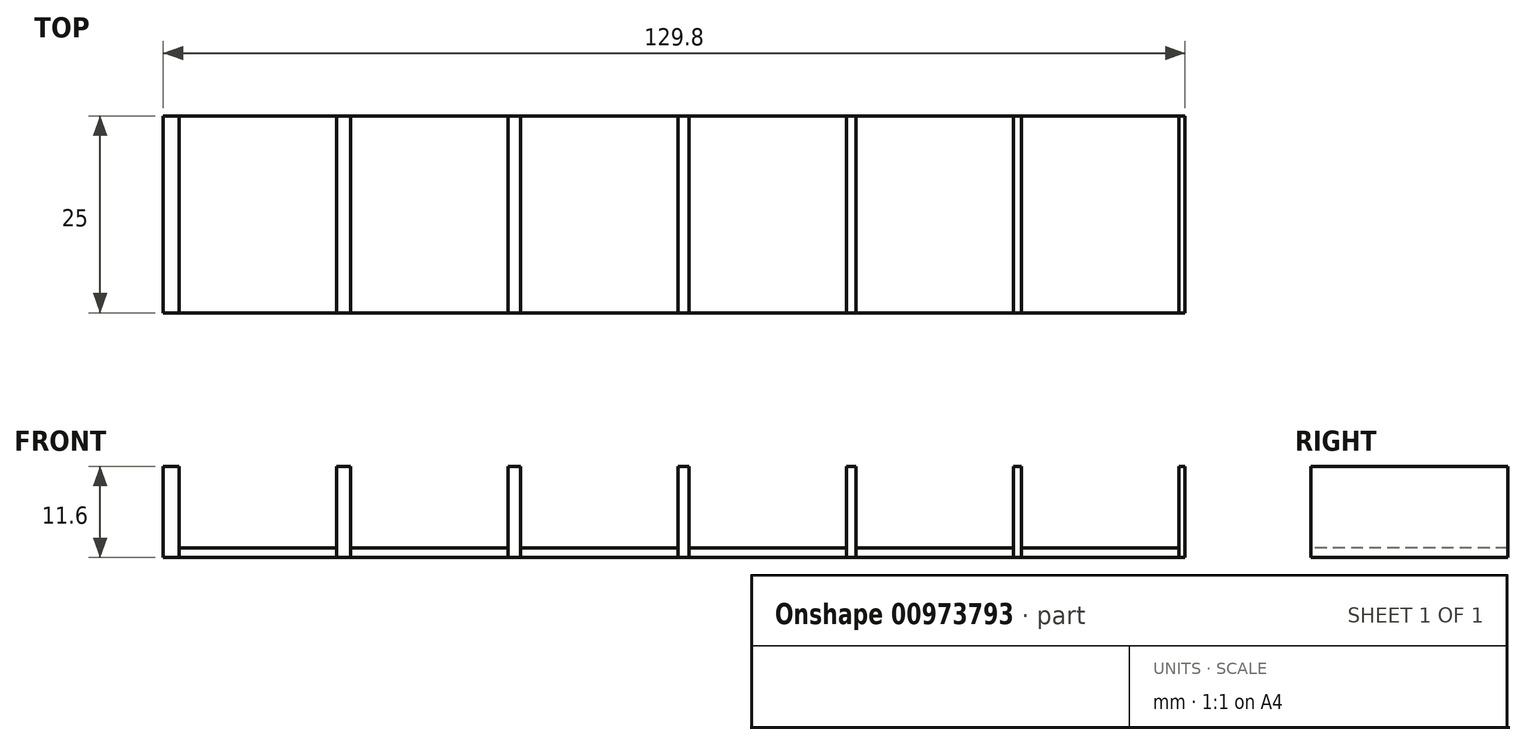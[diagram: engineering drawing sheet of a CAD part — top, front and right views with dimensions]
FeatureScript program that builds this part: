
annotation { "Feature Type Name" : "Feature", "Feature Type Description" : "" }
export const myFeature = defineFeature(function(context is Context, id is Id, definition is map)
    precondition{}
    {
        {
            var Q0;
            Q0=qCreatedBy(makeId("Top.planeOp"),FACE);
            var sketch = newSketch(context, id + "F0", { "sketchPlane" : qUnion([Q0])});
            skLineSegment(sketch, "E0.bottom", {"start": v(0, 0) * mm, "end": v(129.8, 0) * mm});
            skLineSegment(sketch, "E0.top", {"start": v(0, -25) * mm, "end": v(129.8, -25) * mm});
            skLineSegment(sketch, "E0.left", {"start": v(0, 0) * mm, "end": v(0, -25) * mm});
            skLineSegment(sketch, "E0.right", {"start": v(129.8, 0) * mm, "end": v(129.8, -25) * mm});
            skLineSegment(sketch, "E1.0", {"start": v(129, 0) * mm, "end": v(129, -25) * mm});
            skLineSegment(sketch, "E2.0", {"start": v(109, 0) * mm, "end": v(109, -25) * mm});
            skLineSegment(sketch, "E3.0", {"start": v(108, 0) * mm, "end": v(108, -25) * mm});
            skLineSegment(sketch, "E4.0", {"start": v(88, 0) * mm, "end": v(88, -25) * mm});
            skLineSegment(sketch, "E5.0", {"start": v(86.8, 0) * mm, "end": v(86.8, -25) * mm});
            skLineSegment(sketch, "E6.0", {"start": v(66.8, 0) * mm, "end": v(66.8, -25) * mm});
            skLineSegment(sketch, "E7.0", {"start": v(65.4, 0) * mm, "end": v(65.4, -25) * mm});
            skLineSegment(sketch, "E8.0", {"start": v(45.4, 0) * mm, "end": v(45.4, -25) * mm});
            skLineSegment(sketch, "E9.0", {"start": v(43.8, 0) * mm, "end": v(43.8, -25) * mm});
            skLineSegment(sketch, "E10.0", {"start": v(23.8, 0) * mm, "end": v(23.8, -25) * mm});
            skLineSegment(sketch, "E11.0", {"start": v(22, 0) * mm, "end": v(22, -25) * mm});
            skLineSegment(sketch, "E12.0", {"start": v(2, 0) * mm, "end": v(2, -25) * mm});
            skSolve(sketch);
        }
        {
            var Q0;
            {var subQ0=sQuery(id+"F0.wireOp",EDGE,"E0.left");Q0=makeQuery(id+"F0.imprint","IMPRINT",FACE,{"disambiguationData":[TD([[makeQuery(id+"F0.imprint","IMPRINT",EDGE,{"derivedFrom":subQ0}),1.0]])]});}
            var Q1;
            {var subQ0=sQuery(id+"F0.wireOp",EDGE,"E10.0");Q1=makeQuery(id+"F0.imprint","IMPRINT",FACE,{"disambiguationData":[TD([[makeQuery(id+"F0.imprint","IMPRINT",EDGE,{"derivedFrom":subQ0}),-1.0]])]});}
            var Q2;
            {var subQ0=sQuery(id+"F0.wireOp",EDGE,"E8.0");Q2=makeQuery(id+"F0.imprint","IMPRINT",FACE,{"disambiguationData":[TD([[makeQuery(id+"F0.imprint","IMPRINT",EDGE,{"derivedFrom":subQ0}),-1.0]])]});}
            var Q3;
            {var subQ0=sQuery(id+"F0.wireOp",EDGE,"E6.0");Q3=makeQuery(id+"F0.imprint","IMPRINT",FACE,{"disambiguationData":[TD([[makeQuery(id+"F0.imprint","IMPRINT",EDGE,{"derivedFrom":subQ0}),-1.0]])]});}
            var Q4;
            {var subQ0=sQuery(id+"F0.wireOp",EDGE,"E4.0");Q4=makeQuery(id+"F0.imprint","IMPRINT",FACE,{"disambiguationData":[TD([[makeQuery(id+"F0.imprint","IMPRINT",EDGE,{"derivedFrom":subQ0}),-1.0]])]});}
            var Q5;
            {var subQ0=sQuery(id+"F0.wireOp",EDGE,"E2.0");Q5=makeQuery(id+"F0.imprint","IMPRINT",FACE,{"disambiguationData":[TD([[makeQuery(id+"F0.imprint","IMPRINT",EDGE,{"derivedFrom":subQ0}),-1.0]])]});}
            var Q6;
            {var subQ0=sQuery(id+"F0.wireOp",EDGE,"E0.right");Q6=makeQuery(id+"F0.imprint","IMPRINT",FACE,{"disambiguationData":[TD([[makeQuery(id+"F0.imprint","IMPRINT",EDGE,{"derivedFrom":subQ0}),-1.0]])]});}
            extrude(context, id + "F1", {"entities" : qUnion([Q0, Q1, Q2, Q3, Q4, Q5, Q6]), "depth" : 11.6 * mm, "offsetDistance" : 25 * mm});
        }
        {
            var Q0;
            {var subQ0=sQuery(id+"F0.wireOp",EDGE,"E11.0");Q0=makeQuery(id+"F0.imprint","IMPRINT",FACE,{"disambiguationData":[TD([[makeQuery(id+"F0.imprint","IMPRINT",EDGE,{"derivedFrom":subQ0}),-1.0]])]});}
            var Q1;
            {var subQ0=sQuery(id+"F0.wireOp",EDGE,"E9.0");Q1=makeQuery(id+"F0.imprint","IMPRINT",FACE,{"disambiguationData":[TD([[makeQuery(id+"F0.imprint","IMPRINT",EDGE,{"derivedFrom":subQ0}),-1.0]])]});}
            var Q2;
            {var subQ0=sQuery(id+"F0.wireOp",EDGE,"E7.0");Q2=makeQuery(id+"F0.imprint","IMPRINT",FACE,{"disambiguationData":[TD([[makeQuery(id+"F0.imprint","IMPRINT",EDGE,{"derivedFrom":subQ0}),-1.0]])]});}
            var Q3;
            {var subQ0=sQuery(id+"F0.wireOp",EDGE,"E5.0");Q3=makeQuery(id+"F0.imprint","IMPRINT",FACE,{"disambiguationData":[TD([[makeQuery(id+"F0.imprint","IMPRINT",EDGE,{"derivedFrom":subQ0}),-1.0]])]});}
            var Q4;
            {var subQ0=sQuery(id+"F0.wireOp",EDGE,"E3.0");Q4=makeQuery(id+"F0.imprint","IMPRINT",FACE,{"disambiguationData":[TD([[makeQuery(id+"F0.imprint","IMPRINT",EDGE,{"derivedFrom":subQ0}),-1.0]])]});}
            var Q5;
            {var subQ0=sQuery(id+"F0.wireOp",EDGE,"E1.0");Q5=makeQuery(id+"F0.imprint","IMPRINT",FACE,{"disambiguationData":[TD([[makeQuery(id+"F0.imprint","IMPRINT",EDGE,{"derivedFrom":subQ0}),-1.0]])]});}
            extrude(context, id + "F2", {"entities" : qUnion([Q0, Q1, Q2, Q3, Q4, Q5]), "depth" : 1.2 * mm, "offsetDistance" : 25 * mm});
        }
    });
